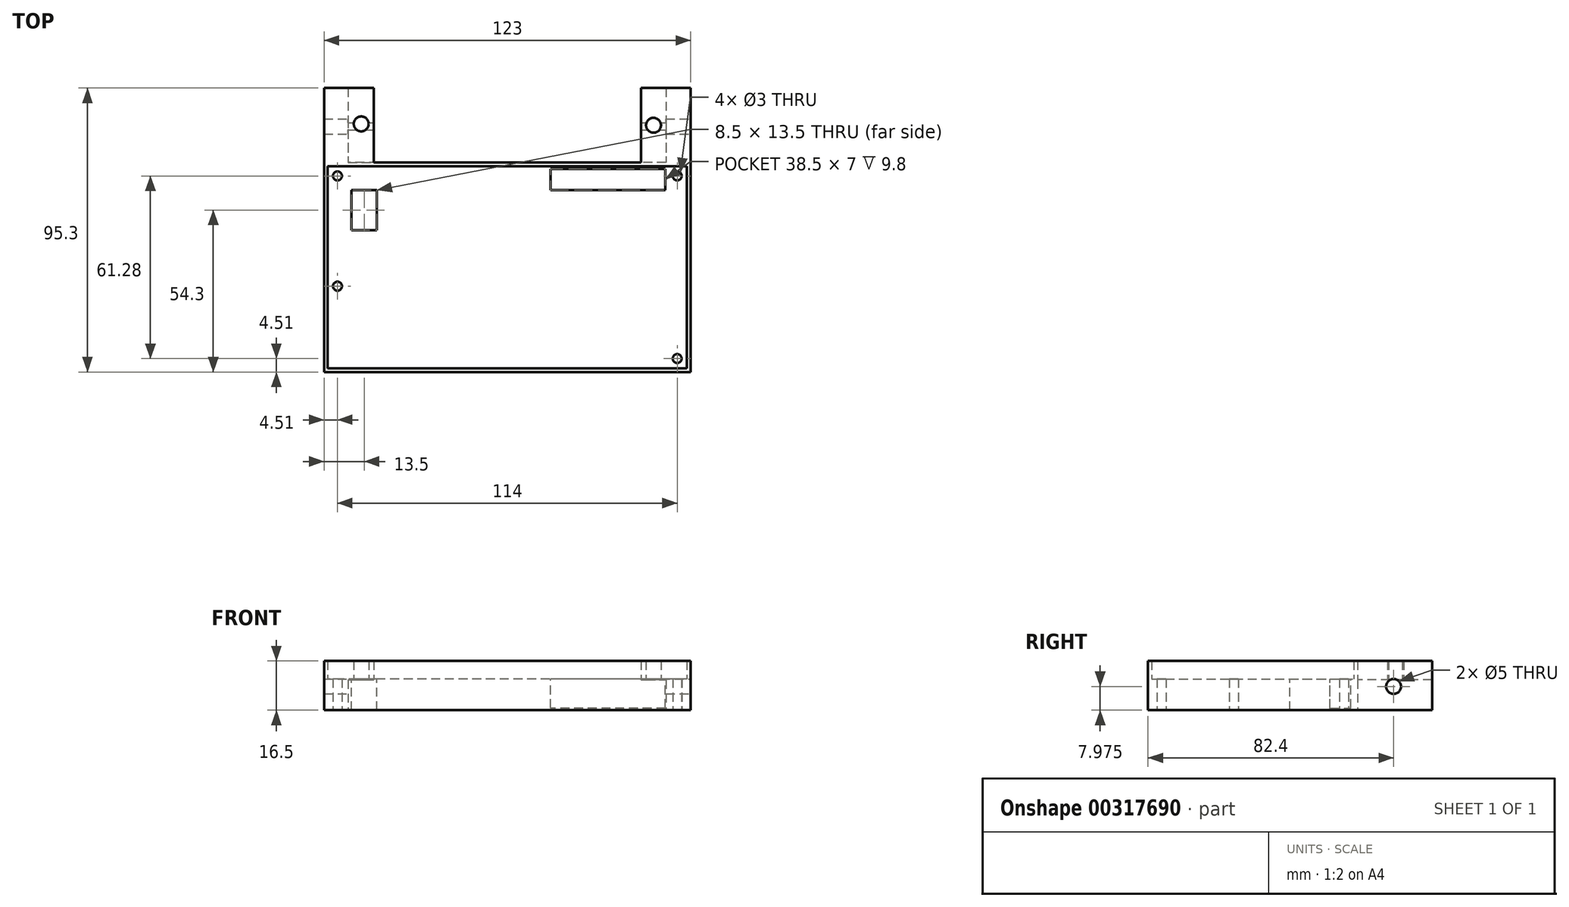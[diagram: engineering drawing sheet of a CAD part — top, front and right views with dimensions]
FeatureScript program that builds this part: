
annotation { "Feature Type Name" : "Feature", "Feature Type Description" : "" }
export const myFeature = defineFeature(function(context is Context, id is Id, definition is map)
    precondition{}
    {
        {
            var Q0;
            Q0=qCreatedBy(makeId("Top.planeOp"),FACE);
            var sketch = newSketch(context, id + "F0", { "sketchPlane" : qUnion([Q0])});
            skLineSegment(sketch, "E0.bottom", {"start": v(60.25, -33.9) * mm, "end": v(-60.25, -33.9) * mm});
            skLineSegment(sketch, "E0.top", {"start": v(60.25, 33.9) * mm, "end": v(-60.25, 33.9) * mm});
            skLineSegment(sketch, "E0.left", {"start": v(60.25, -33.9) * mm, "end": v(60.25, 33.9) * mm});
            skLineSegment(sketch, "E0.right", {"start": v(-60.25, -33.9) * mm, "end": v(-60.25, 33.9) * mm});
            skPoint(sketch, "E0.middle", {"position": v(0, 0) * mm});
            skCircle(sketch, "E1", {"center": v(-57, 30.64) * mm, "radius": 1.5 * mm});
            skCircle(sketch, "E2", {"center": v(57.01, 30.64) * mm, "radius": 1.5 * mm});
            skCircle(sketch, "E3", {"center": v(-57, -6.36) * mm, "radius": 1.5 * mm});
            skCircle(sketch, "E4", {"center": v(57, -30.64) * mm, "radius": 1.5 * mm});
            skLineSegment(sketch, "E5.bottom", {"start": v(61.5, -35.15) * mm, "end": v(-61.5, -35.15) * mm});
            skLineSegment(sketch, "E5.top", {"start": v(61.5, 35.15) * mm, "end": v(-61.5, 35.15) * mm});
            skLineSegment(sketch, "E5.left", {"start": v(61.5, -35.15) * mm, "end": v(61.5, 35.15) * mm});
            skLineSegment(sketch, "E5.right", {"start": v(-61.5, -35.15) * mm, "end": v(-61.5, 35.15) * mm});
            skSolve(sketch);
        }
        {
            var Q0;
            Q0=makeQuery(id+"F0.imprint","IMPRINT",FACE,{"disambiguationData":[TD([[makeQuery(id+"F0.imprint","IMPRINT",EDGE,{"derivedFrom":sQuery(id+"F0.wireOp",EDGE,"E0.bottom")}),1.0]])]});
            extrude(context, id + "F1", {"entities" : qUnion([Q0]), "depth" : 16.5 * mm});
        }
        {
            var Q0;
            Q0=makeQuery(id+"F0.imprint","IMPRINT",FACE,{"disambiguationData":[TD([[makeQuery(id+"F0.imprint","IMPRINT",EDGE,{"derivedFrom":sQuery(id+"F0.wireOp",EDGE,"E0.bottom")}),-1.0]])]});
            extrude(context, id + "F2", {"entities" : qUnion([Q0]), "operationType" : NewBodyOperationType.ADD, "depth" : 10.5 * mm});
        }
        {
            var Q0;
            Q0=makeQuery(id+"F2.opExtrude","CAP_FACE",FACE,{"disambiguationData":[OSD([sQuery(id+"F0.wireOp",EDGE,"E0.bottom"),sQuery(id+"F0.wireOp",EDGE,"E0.top"),sQuery(id+"F0.wireOp",EDGE,"E0.left"),sQuery(id+"F0.wireOp",EDGE,"E0.right"),sQuery(id+"F0.wireOp",EDGE,"E1"),sQuery(id+"F0.wireOp",EDGE,"E2"),sQuery(id+"F0.wireOp",EDGE,"E3"),sQuery(id+"F0.wireOp",EDGE,"E4")])],"isStart":false});
            var sketch = newSketch(context, id + "F3", { "sketchPlane" : qUnion([Q0])});
            skLineSegment(sketch, "E6.bottom", {"start": v(53.01, 25.95) * mm, "end": v(14.51, 25.95) * mm});
            skLineSegment(sketch, "E6.top", {"start": v(53.01, 32.95) * mm, "end": v(14.51, 32.95) * mm});
            skLineSegment(sketch, "E6.left", {"start": v(53.01, 25.95) * mm, "end": v(53.01, 32.95) * mm});
            skLineSegment(sketch, "E6.right", {"start": v(14.51, 25.95) * mm, "end": v(14.51, 32.95) * mm});
            skPoint(sketch, "E6.middle", {"position": v(33.76, 29.45) * mm});
            skLineSegment(sketch, "E7.bottom", {"start": v(-43.75, 12.4) * mm, "end": v(-52.25, 12.4) * mm});
            skLineSegment(sketch, "E7.top", {"start": v(-43.75, 25.9) * mm, "end": v(-52.25, 25.9) * mm});
            skLineSegment(sketch, "E7.left", {"start": v(-43.75, 12.4) * mm, "end": v(-43.75, 25.9) * mm});
            skLineSegment(sketch, "E7.right", {"start": v(-52.25, 12.4) * mm, "end": v(-52.25, 25.9) * mm});
            skPoint(sketch, "E7.middle", {"position": v(-48, 19.15) * mm});
            skSolve(sketch);
        }
        {
            var Q0;
            Q0=makeQuery(id+"F3.imprint","IMPRINT",FACE,{"disambiguationData":[TD([[makeQuery(id+"F3.imprint","IMPRINT",EDGE,{"derivedFrom":sQuery(id+"F3.wireOp",EDGE,"E6.bottom")}),-1.0]])]});
            extrude(context, id + "F4", {"entities" : qUnion([Q0]), "operationType" : NewBodyOperationType.REMOVE, "oppositeDirection" : true, "depth" : 9.8 * mm});
        }
        {
            var Q0;
            Q0=makeQuery(id+"F3.imprint","IMPRINT",FACE,{"disambiguationData":[TD([[makeQuery(id+"F3.imprint","IMPRINT",EDGE,{"derivedFrom":sQuery(id+"F3.wireOp",EDGE,"E7.bottom")}),-1.0]])]});
            extrude(context, id + "F5", {"entities" : qUnion([Q0]), "operationType" : NewBodyOperationType.REMOVE, "oppositeDirection" : true, "depth" : 25 * mm});
        }
        {
            var Q0;
            Q0=makeQuery(id+"F1.opExtrude","SWEPT_FACE",FACE,{"disambiguationData":[OSD([sQuery(id+"F0.wireOp",EDGE,"E5.top")])]});
            var sketch = newSketch(context, id + "F6", { "sketchPlane" : qUnion([Q0])});
            skLineSegment(sketch, "E8.bottom", {"start": v(-61.5, 16.5) * mm, "end": v(-53.23, 16.5) * mm});
            skLineSegment(sketch, "E8.top", {"start": v(-61.5, 0) * mm, "end": v(-53.23, 0) * mm});
            skLineSegment(sketch, "E8.left", {"start": v(-61.5, 16.5) * mm, "end": v(-61.5, 0) * mm});
            skLineSegment(sketch, "E8.right", {"start": v(-53.23, 16.5) * mm, "end": v(-53.23, 0) * mm});
            skLineSegment(sketch, "E9.bottom", {"start": v(-53.23, 16.5) * mm, "end": v(-44.86, 16.5) * mm});
            skLineSegment(sketch, "E9.top", {"start": v(-53.23, 10.17) * mm, "end": v(-44.86, 10.17) * mm});
            skLineSegment(sketch, "E9.left", {"start": v(-53.23, 16.5) * mm, "end": v(-53.23, 10.17) * mm});
            skLineSegment(sketch, "E9.right", {"start": v(-44.86, 16.5) * mm, "end": v(-44.86, 10.17) * mm});
            skLineSegment(sketch, "E10.bottom", {"start": v(61.5, 16.5) * mm, "end": v(53.43, 16.5) * mm});
            skLineSegment(sketch, "E10.top", {"start": v(61.5, 0) * mm, "end": v(53.43, 0) * mm});
            skLineSegment(sketch, "E10.left", {"start": v(61.5, 16.5) * mm, "end": v(61.5, 0) * mm});
            skLineSegment(sketch, "E10.right", {"start": v(53.43, 16.5) * mm, "end": v(53.43, 0) * mm});
            skLineSegment(sketch, "E11.bottom", {"start": v(53.43, 16.5) * mm, "end": v(44.86, 16.5) * mm});
            skLineSegment(sketch, "E11.top", {"start": v(53.43, 10.17) * mm, "end": v(44.86, 10.17) * mm});
            skLineSegment(sketch, "E11.left", {"start": v(53.43, 16.5) * mm, "end": v(53.43, 10.17) * mm});
            skLineSegment(sketch, "E11.right", {"start": v(44.86, 16.5) * mm, "end": v(44.86, 10.17) * mm});
            skSolve(sketch);
        }
        {
            var Q0;
            Q0=makeQuery(id+"F6.imprint","IMPRINT",FACE,{"disambiguationData":[TD([[makeQuery(id+"F6.imprint","IMPRINT",EDGE,{"derivedFrom":sQuery(id+"F6.wireOp",EDGE,"E9.bottom")}),-1.0]])]});
            var Q1;
            Q1=makeQuery(id+"F6.imprint","IMPRINT",FACE,{"disambiguationData":[TD([[makeQuery(id+"F6.imprint","IMPRINT",EDGE,{"derivedFrom":sQuery(id+"F6.wireOp",EDGE,"E8.bottom")}),-1.0]])]});
            var Q2;
            Q2=makeQuery(id+"F6.imprint","IMPRINT",FACE,{"disambiguationData":[TD([[makeQuery(id+"F6.imprint","IMPRINT",EDGE,{"derivedFrom":sQuery(id+"F6.wireOp",EDGE,"E11.bottom")}),-1.0]])]});
            var Q3;
            Q3=makeQuery(id+"F6.imprint","IMPRINT",FACE,{"disambiguationData":[TD([[makeQuery(id+"F6.imprint","IMPRINT",EDGE,{"derivedFrom":sQuery(id+"F6.wireOp",EDGE,"E10.bottom")}),-1.0]])]});
            extrude(context, id + "F7", {"entities" : qUnion([Q0, Q1, Q2, Q3]), "operationType" : NewBodyOperationType.ADD, "depth" : 25 * mm});
        }
        {
            var Q0;
            Q0=makeQuery(id+"F7.opExtrude","SWEPT_FACE",FACE,{"disambiguationData":[OSD([sQuery(id+"F6.wireOp",EDGE,"E11.top")])]});
            var sketch = newSketch(context, id + "F8", { "sketchPlane" : qUnion([Q0])});
            skCircle(sketch, "E12", {"center": v(-49.02, -48.11) * mm, "radius": 2.94 * mm});
            skSolve(sketch);
        }
        {
            var Q0;
            Q0=sQuery(id+"F8.wireOp",VERTEX,"E12.center");
            var Q1;
            Q1=makeQuery(id+"F1.opExtrude","SWEPT_BODY",BODY,{"disambiguationData":[OSD([sQuery(id+"F0.wireOp",EDGE,"E0.bottom"),sQuery(id+"F0.wireOp",EDGE,"E0.top"),sQuery(id+"F0.wireOp",EDGE,"E0.left"),sQuery(id+"F0.wireOp",EDGE,"E0.right"),sQuery(id+"F0.wireOp",EDGE,"E5.bottom"),sQuery(id+"F0.wireOp",EDGE,"E5.top"),sQuery(id+"F0.wireOp",EDGE,"E5.left"),sQuery(id+"F0.wireOp",EDGE,"E5.right")])]});
            hole(context, id + "F9", {"style" : HoleStyle.SIMPLE, "endStyle" : HoleEndStyle.THROUGH, "holeDiameter" : 5 * mm, "tappedDepth" : 12 * mm, "tapClearance" : 3, "startFromSketch" : true, "locations" : qUnion([Q0]), "scope" : qUnion([Q1])});
        }
        {
            var Q0;
            Q0=makeQuery(id+"F7.opExtrude","SWEPT_FACE",FACE,{"disambiguationData":[OSD([sQuery(id+"F6.wireOp",EDGE,"E9.top")])]});
            var sketch = newSketch(context, id + "F10", { "sketchPlane" : qUnion([Q0])});
            skCircle(sketch, "E13", {"center": v(49.04, -47.65) * mm, "radius": 2.6 * mm});
            skPoint(sketch, "E13.centerSnap0", {"position": v(44.86, -47.65) * mm});
            skSolve(sketch);
        }
        {
            var Q0;
            Q0=sQuery(id+"F10.wireOp",VERTEX,"E13.center");
            var Q1;
            Q1=makeQuery(id+"F1.opExtrude","SWEPT_BODY",BODY,{"disambiguationData":[OSD([sQuery(id+"F0.wireOp",EDGE,"E0.bottom"),sQuery(id+"F0.wireOp",EDGE,"E0.top"),sQuery(id+"F0.wireOp",EDGE,"E0.left"),sQuery(id+"F0.wireOp",EDGE,"E0.right"),sQuery(id+"F0.wireOp",EDGE,"E5.bottom"),sQuery(id+"F0.wireOp",EDGE,"E5.top"),sQuery(id+"F0.wireOp",EDGE,"E5.left"),sQuery(id+"F0.wireOp",EDGE,"E5.right")])]});
            hole(context, id + "F11", {"style" : HoleStyle.SIMPLE, "endStyle" : HoleEndStyle.THROUGH, "holeDiameter" : 5 * mm, "tappedDepth" : 12 * mm, "tapClearance" : 3, "startFromSketch" : true, "locations" : qUnion([Q0]), "scope" : qUnion([Q1])});
        }
        {
            var Q0;
            Q0=makeQuery(id+"F7.boolean.opBoolean","MERGE",FACE,{"derivedFrom":[makeQuery(id+"F1.opExtrude","SWEPT_FACE",FACE,{"disambiguationData":[OSD([sQuery(id+"F0.wireOp",EDGE,"E5.left")])]}),makeQuery(id+"F7.opExtrude","SWEPT_FACE",FACE,{"disambiguationData":[OSD([sQuery(id+"F6.wireOp",EDGE,"E8.left")])]})]});
            var sketch = newSketch(context, id + "F12", { "sketchPlane" : qUnion([Q0])});
            skCircle(sketch, "E14", {"center": v(47.25, 7.97) * mm, "radius": 2.6 * mm});
            skSolve(sketch);
        }
        {
            var Q0;
            Q0=sQuery(id+"F12.wireOp",VERTEX,"E14.center");
            var Q1;
            Q1=makeQuery(id+"F1.opExtrude","SWEPT_BODY",BODY,{"disambiguationData":[OSD([sQuery(id+"F0.wireOp",EDGE,"E0.bottom"),sQuery(id+"F0.wireOp",EDGE,"E0.top"),sQuery(id+"F0.wireOp",EDGE,"E0.left"),sQuery(id+"F0.wireOp",EDGE,"E0.right"),sQuery(id+"F0.wireOp",EDGE,"E5.bottom"),sQuery(id+"F0.wireOp",EDGE,"E5.top"),sQuery(id+"F0.wireOp",EDGE,"E5.left"),sQuery(id+"F0.wireOp",EDGE,"E5.right")])]});
            hole(context, id + "F13", {"style" : HoleStyle.SIMPLE, "endStyle" : HoleEndStyle.THROUGH, "holeDiameter" : 5 * mm, "tappedDepth" : 12 * mm, "tapClearance" : 3, "startFromSketch" : true, "locations" : qUnion([Q0]), "scope" : qUnion([Q1])});
        }
    });
